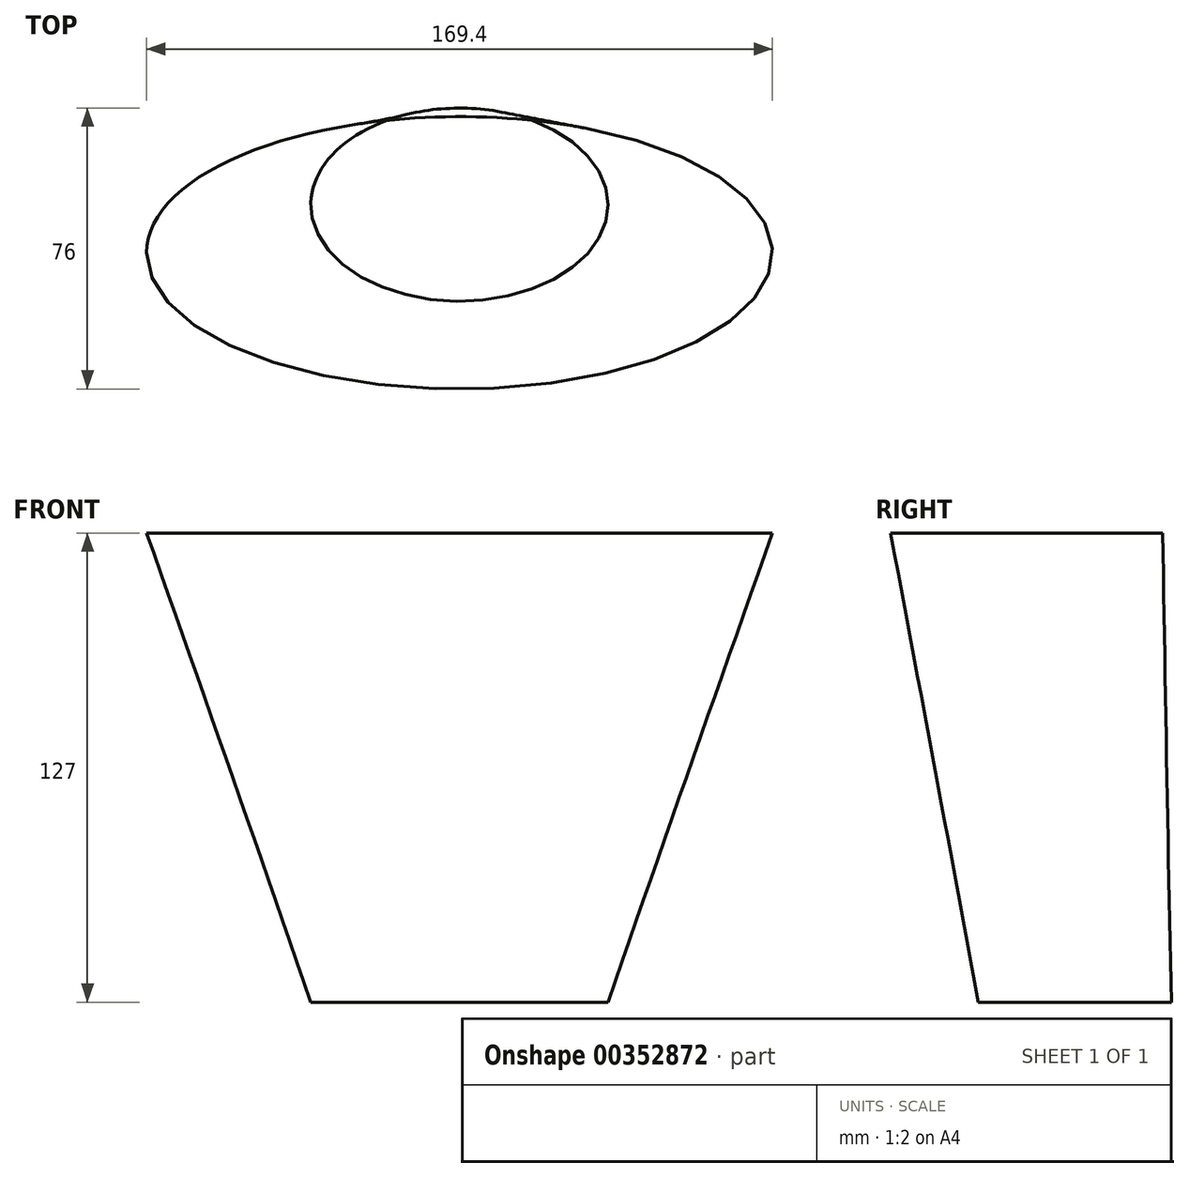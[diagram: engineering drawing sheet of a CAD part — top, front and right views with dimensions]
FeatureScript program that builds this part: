
annotation { "Feature Type Name" : "Feature", "Feature Type Description" : "" }
export const myFeature = defineFeature(function(context is Context, id is Id, definition is map)
    precondition{}
    {
        {
            var Q0;
            Q0=qCreatedBy(makeId("Top.planeOp"),FACE);
            var sketch = newSketch(context, id + "F0", { "sketchPlane" : qUnion([Q0])});
            skEllipse(sketch, "E0", {"center": v(0, 0) * mm, "majorRadius": 40.23 * mm, "minorRadius": 26.13 * mm, "majorAxis": v(1, 0)});
            skSolve(sketch);
        }
        {
            var Q0;
            Q0=qCreatedBy(makeId("Top.planeOp"),FACE);
            var sketch = newSketch(context, id + "F1", { "sketchPlane" : qUnion([Q0])});
            skLineSegment(sketch, "E1.bottom", {"start": v(-52.1, 59.36) * mm, "end": v(53.58, 59.36) * mm});
            skLineSegment(sketch, "E1.top", {"start": v(-52.1, -66.58) * mm, "end": v(53.58, -66.58) * mm});
            skLineSegment(sketch, "E1.left", {"start": v(-52.1, 59.36) * mm, "end": v(-52.1, -66.58) * mm});
            skLineSegment(sketch, "E1.right", {"start": v(53.58, 59.36) * mm, "end": v(53.58, -66.58) * mm});
            skSolve(sketch);
        }
        {
            var Q0;
            Q0=makeQuery(id+"F1.imprint","IMPRINT",FACE,{"disambiguationData":[TD([[makeQuery(id+"F1.imprint","IMPRINT",EDGE,{"derivedFrom":sQuery(id+"F1.wireOp",EDGE,"E1.bottom")}),-1.0]])]});
            cPlane(context, id + "F2", {"entities" : qUnion([Q0]), "cplaneType" : CPlaneType.OFFSET, "offset" : 127 * mm, "width" : 152.4 * mm, "height" : 152.4 * mm});
        }
        {
            var Q0;
            Q0=qCreatedBy(id+"F2.planeOp",FACE);
            var sketch = newSketch(context, id + "F3", { "sketchPlane" : qUnion([Q0])});
            skEllipse(sketch, "E2", {"center": v(0, -13.03) * mm, "majorRadius": 84.7 * mm, "minorRadius": 36.84 * mm, "majorAxis": v(-1, 0)});
            skSolve(sketch);
        }
        {
            var Q0;
            Q0=sQuery(id+"F3.wireOp",EDGE,"E2");
            var Q1;
            Q1=sQuery(id+"F0.wireOp",EDGE,"E0");
            loft(context, id + "F4", {"bodyType" : ToolBodyType.SURFACE, "wireProfilesArray" : [{ "wireProfileEntities" : qUnion([Q0]) }, { "wireProfileEntities" : qUnion([Q1]) }]});
        }
    });
